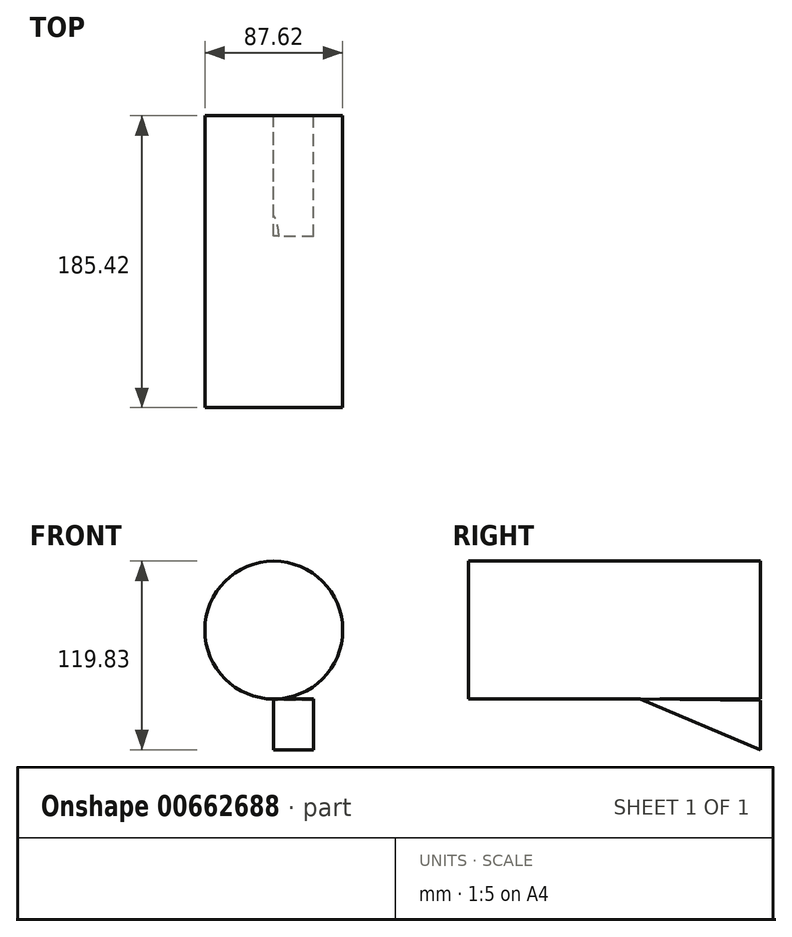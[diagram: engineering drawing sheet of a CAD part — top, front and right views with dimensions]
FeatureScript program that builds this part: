
annotation { "Feature Type Name" : "Feature", "Feature Type Description" : "" }
export const myFeature = defineFeature(function(context is Context, id is Id, definition is map)
    precondition{}
    {
        {
            var Q0;
            Q0=qCreatedBy(makeId("Front.planeOp"),FACE);
            var sketch = newSketch(context, id + "F0", { "sketchPlane" : qUnion([Q0])});
            skCircle(sketch, "E0", {"center": v(0, 0) * mm, "radius": 43.8 * mm});
            skSolve(sketch);
        }
        {
            var Q0;
            Q0=makeQuery(id+"F0.imprint","IMPRINT",FACE,{"disambiguationData":[TD([[makeQuery(id+"F0.imprint","IMPRINT",EDGE,{"derivedFrom":sQuery(id+"F0.wireOp",EDGE,"E0")}),1.0]])]});
            extrude(context, id + "F1", {"entities" : qUnion([Q0]), "depth" : 90.68 * mm, "offsetDistance" : 25.4 * mm});
        }
        {
            var Q0;
            Q0=makeQuery(id+"F1.opExtrude","CAP_FACE",FACE,{"disambiguationData":[OSD([sQuery(id+"F0.wireOp",EDGE,"E0")])],"isStart":false});
            extrude(context, id + "F2", {"entities" : qUnion([Q0]), "operationType" : NewBodyOperationType.ADD, "depth" : 94.74 * mm, "offsetDistance" : 25.4 * mm});
        }
        {
            var Q0;
            Q0=qCreatedBy(makeId("Top.planeOp"),FACE);
            var sketch = newSketch(context, id + "F3", { "sketchPlane" : qUnion([Q0])});
            skLineSegment(sketch, "E1", {"start": v(-44.45, -76.31) * mm, "end": v(-74.67, 0) * mm});
            skLineSegment(sketch, "E2", {"start": v(-74.67, 0) * mm, "end": v(-43.55, 0) * mm});
            skLineSegment(sketch, "E3", {"start": v(-44.45, -76.31) * mm, "end": v(-43.55, 0) * mm});
            skSolve(sketch);
        }
        {
            var Q0;
            Q0=qCreatedBy(makeId("Right.planeOp"),FACE);
            var sketch = newSketch(context, id + "F4", { "sketchPlane" : qUnion([Q0])});
            skLineSegment(sketch, "E4", {"start": v(-76.63, -43.67) * mm, "end": v(0, -76.02) * mm});
            skLineSegment(sketch, "E5", {"start": v(0, -76.02) * mm, "end": v(0, -44.5) * mm});
            skLineSegment(sketch, "E6", {"start": v(-76.63, -43.67) * mm, "end": v(0, -44.5) * mm});
            skSolve(sketch);
        }
        {
            var Q0;
            Q0=makeQuery(id+"F2.opExtrude","CAP_FACE",FACE,{"disambiguationData":[OSD([sQuery(id+"F0.wireOp",EDGE,"E0")])],"isStart":false});
            var sketch = newSketch(context, id + "F5", { "sketchPlane" : qUnion([Q0])});
            skSolve(sketch);
        }
        {
            var Q0;
            Q0=makeQuery(id+"F5.imprint","IMPRINT",FACE,{"disambiguationData":[TD([[makeQuery(id+"F5.imprint","IMPRINT",EDGE,{"derivedFrom":makeQuery(id+"F2.opExtrude","CAP_EDGE",EDGE,{"disambiguationData":[OSD([sQuery(id+"F0.wireOp",EDGE,"E0")])],"isStart":false})}),1.0]])]});
            var sketch = newSketch(context, id + "F6", { "sketchPlane" : qUnion([Q0])});
            skSolve(sketch);
        }
        {
            var Q0;
            Q0 = qSketchRegion(id + "F6", true);
            var Q1;
            Q1=makeQuery(id+"F4.imprint","IMPRINT",FACE,{"disambiguationData":[TD([[makeQuery(id+"F4.imprint","IMPRINT",EDGE,{"derivedFrom":sQuery(id+"F4.wireOp",EDGE,"E4")}),1.0]])]});
            extrude(context, id + "F7", {"entities" : qUnion([Q0, Q1]), "operationType" : NewBodyOperationType.ADD, "depth" : 25.4 * mm, "offsetDistance" : 25.4 * mm});
        }
        {
            var Q0;
            Q0=sQuery(id+"F3.wireOp",EDGE,"E1");
            var Q1;
            Q1=sQuery(id+"F3.wireOp",EDGE,"E3");
            var Q2;
            Q2=sQuery(id+"F3.wireOp",EDGE,"E2");
            extrude(context, id + "F8", {"bodyType" : ToolBodyType.SURFACE, "surfaceEntities" : qUnion([Q0, Q1, Q2]), "depth" : 25.4 * mm, "offsetDistance" : 25.4 * mm});
        }
    });
